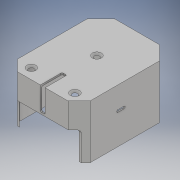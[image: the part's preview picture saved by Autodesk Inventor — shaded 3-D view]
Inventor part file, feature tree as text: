
AUTODESK INVENTOR PART (.ipt)
format: ipt  version: 2017 (Build 210142000, 142)  size: 456,704 bytes
history: native  units: mm
features: extrude x9, sketch x7, other x5, fillet x4, hole x3
ambient origin geometry x8: Origin, YZ Plane, XZ Plane, XY Plane, X Axis, Y Axis, Z Axis, Center Point
bodies: Body1 (feature_tree)
feature tree (28):
  other  "Твердое тело1"
  sketch  "Эскиз1"
  extrude  "Выдавливание1"  Depth=58.6mm
  extrude  "Выдавливание2"  Depth=77.0mm
  fillet  "Сопряжение1"  Radius=11.0mm
  extrude  "Выдавливание3"  Depth=11.0mm
  extrude  "Выдавливание4"  Depth=8.5mm
  extrude  "Выдавливание5"  Depth=8.5mm
  other  "Комбинировать1"
  hole  "Отверстие4"  [1 undecoded]
  hole  "Отверстие5"  [1 undecoded]
  hole  "Отверстие6"  [1 undecoded]
  fillet  "Сопряжение2"  Radius=11.0mm
  fillet  "Сопряжение3"  Radius=1.2mm
  extrude  "Выдавливание6"  Depth=1.5mm TaperAngle=0.0deg
  extrude  "Выдавливание7"  Depth=43.5mm TaperAngle=0.0deg
  extrude  "Выдавливание8"  Depth=1.0mm
  other  "Комбинировать2"
  fillet  "Сопряжение4"  Radius=4.0mm
  extrude  "Выдавливание10"  Depth=17.0mm
  other  "Твердое тело2"
  sketch  "Эскиз2"
  sketch  "Эскиз3"
  sketch  "Эскиз4"
  other  "Твердое тело3"
  sketch  "Эскиз5"
  sketch  "Эскиз6"
  sketch  "Эскиз8"
note: 3 required parameter values undecoded (feature->parameter linkage not recoverable at this tier; creation-order binding heuristic only, values carry confidence <= 0.55)
